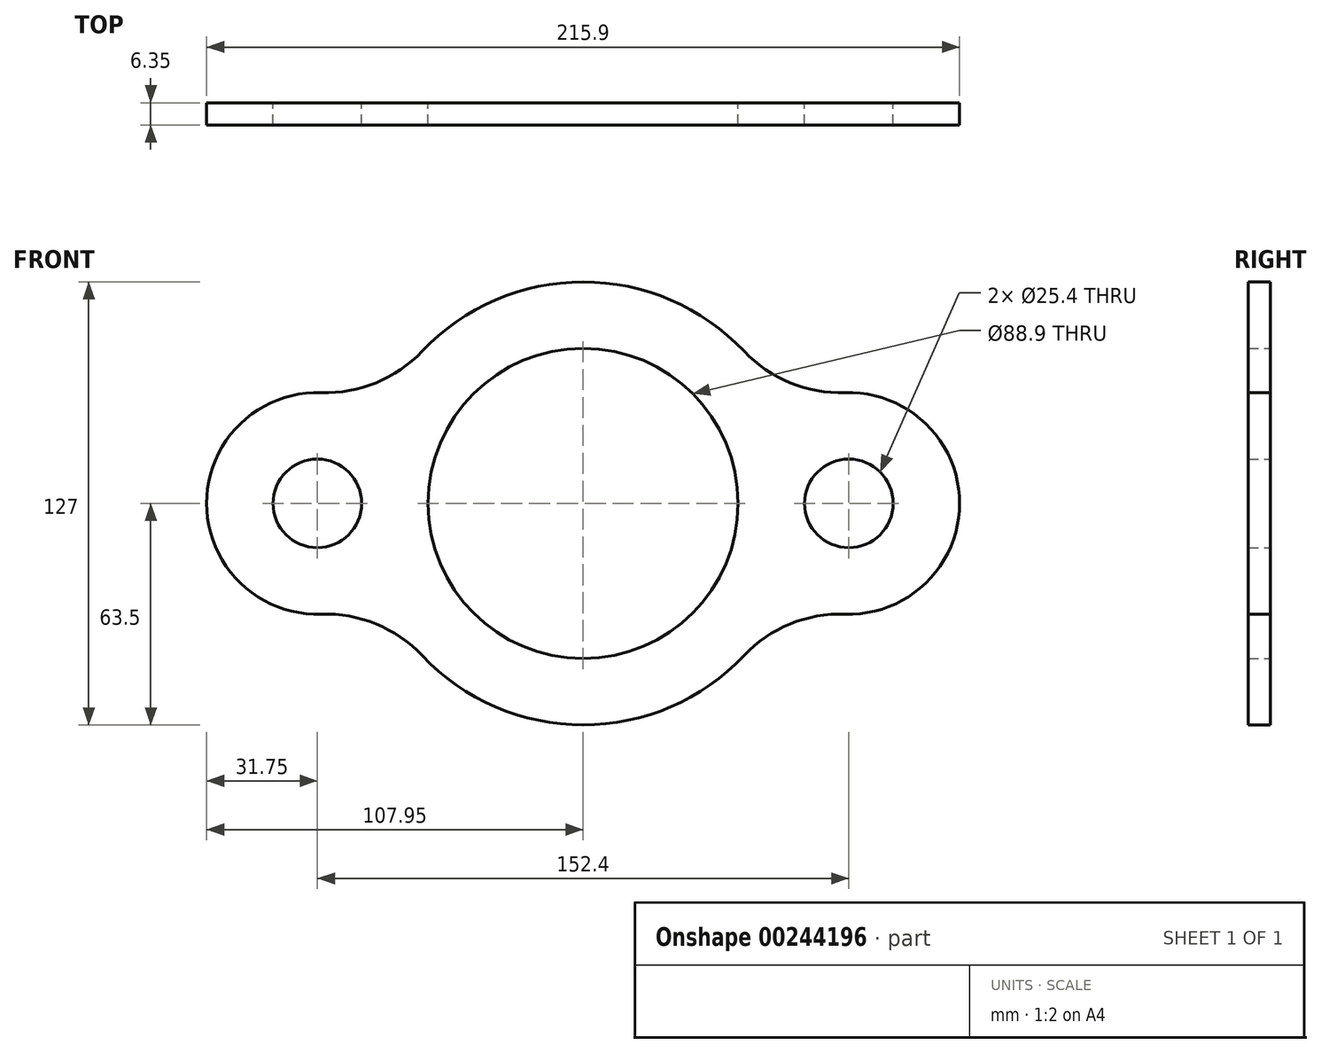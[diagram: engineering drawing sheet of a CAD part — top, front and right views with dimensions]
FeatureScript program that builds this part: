
annotation { "Feature Type Name" : "Feature", "Feature Type Description" : "" }
export const myFeature = defineFeature(function(context is Context, id is Id, definition is map)
    precondition{}
    {
        {
            var Q0;
            Q0=qCreatedBy(makeId("Front.planeOp"),FACE);
            var sketch = newSketch(context, id + "F0", { "sketchPlane" : qUnion([Q0])});
            skCircle(sketch, "E0", {"center": v(0, 0) * mm, "radius": 44.45 * mm});
            skCircle(sketch, "E1", {"center": v(76.2, 0) * mm, "radius": 12.7 * mm});
            skArc(sketch, "E2", {"start": v(75.12, -31.73) * mm, "mid": v(107.95, 0) * mm, "end": v(75.12, 31.73) * mm});
            skArc(sketch, "E3", {"start": v(-75.12, 31.73) * mm, "mid": v(-107.95, 0) * mm, "end": v(-75.12, -31.73) * mm});
            skCircle(sketch, "E4", {"center": v(-76.2, 0) * mm, "radius": 12.7 * mm});
            skArc(sketch, "E5", {"start": v(-46.14, -43.63) * mm, "mid": v(0, -63.5) * mm, "end": v(46.14, -43.63) * mm});
            skArc(sketch, "E6.trimOffspring", {"start": v(46.14, 43.63) * mm, "mid": v(0, 63.5) * mm, "end": v(-46.14, 43.63) * mm});
            skPoint(sketch, "E7.visualSharp", {"position": v(-57.94, 25.98) * mm});
            skArc(sketch, "E7.filletArc", {"start": v(-75.12, 31.73) * mm, "mid": v(-59.35, 34.56) * mm, "end": v(-46.14, 43.63) * mm});
            skPoint(sketch, "E8.visualSharp", {"position": v(-57.94, -25.98) * mm});
            skArc(sketch, "E8.filletArc", {"start": v(-46.14, -43.63) * mm, "mid": v(-59.35, -34.56) * mm, "end": v(-75.12, -31.73) * mm});
            skPoint(sketch, "E9.visualSharp", {"position": v(57.94, -25.98) * mm});
            skArc(sketch, "E9.filletArc", {"start": v(75.12, -31.73) * mm, "mid": v(59.35, -34.56) * mm, "end": v(46.14, -43.63) * mm});
            skPoint(sketch, "E10.visualSharp", {"position": v(57.94, 25.98) * mm});
            skArc(sketch, "E10.filletArc", {"start": v(46.14, 43.63) * mm, "mid": v(59.35, 34.56) * mm, "end": v(75.12, 31.73) * mm});
            skSolve(sketch);
        }
        {
            var Q0;
            Q0 = qSketchRegion(id + "F0", true);
            extrude(context, id + "F1", {"entities" : qUnion([Q0]), "depth" : 6.35 * mm});
        }
    });
